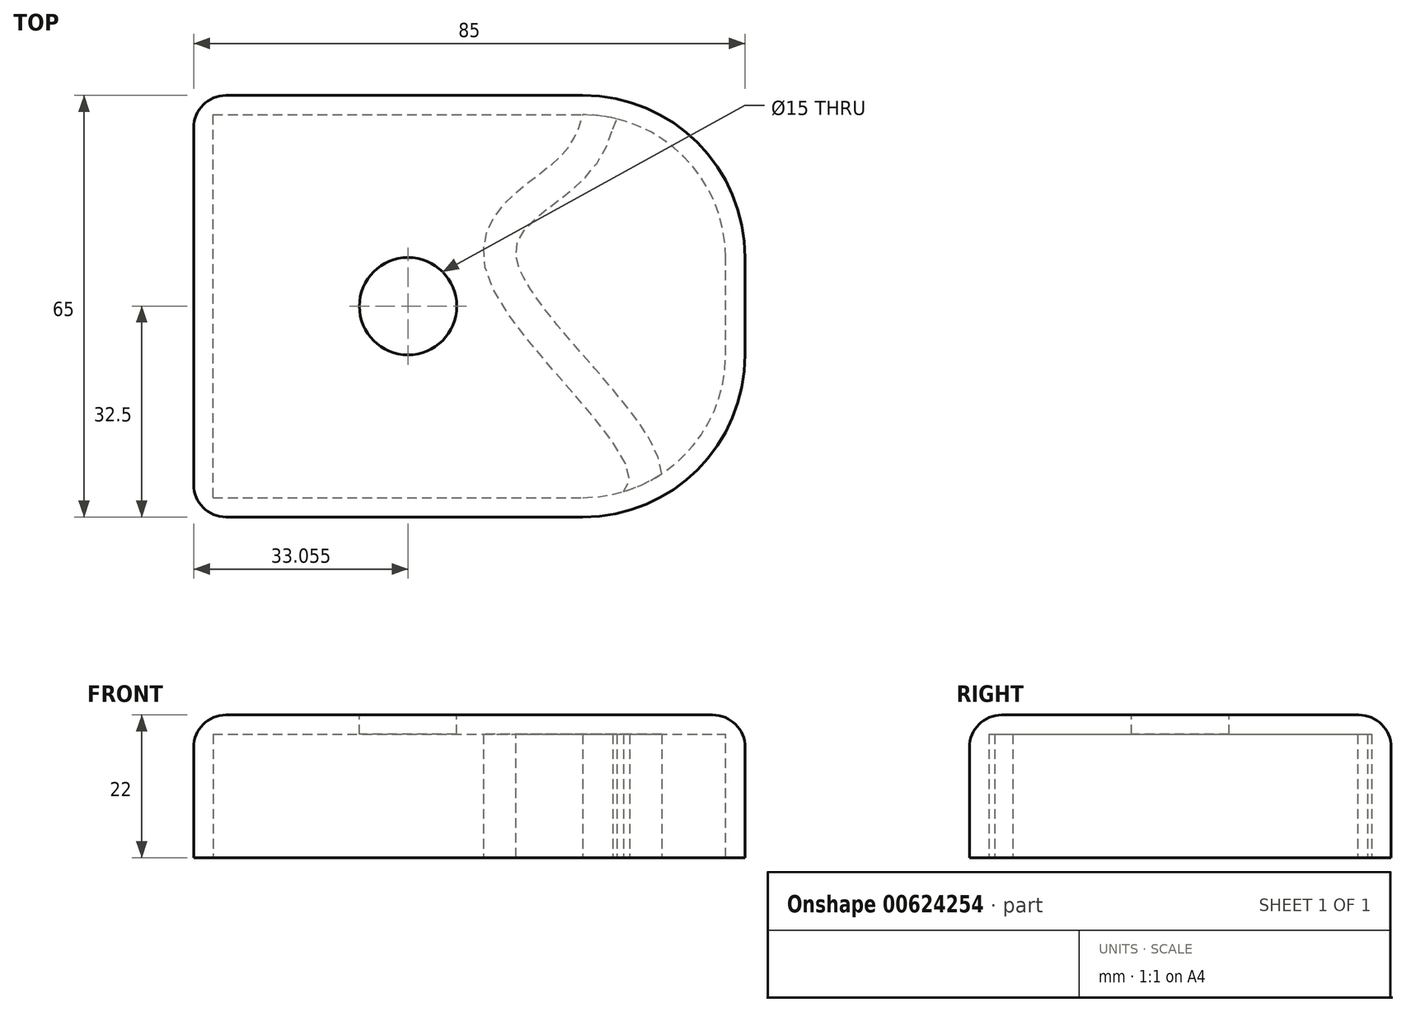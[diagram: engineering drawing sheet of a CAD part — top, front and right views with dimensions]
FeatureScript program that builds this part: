
annotation { "Feature Type Name" : "Feature", "Feature Type Description" : "" }
export const myFeature = defineFeature(function(context is Context, id is Id, definition is map)
    precondition{}
    {
        {
            var Q0;
            Q0=qCreatedBy(makeId("Top.planeOp"),FACE);
            var sketch = newSketch(context, id + "F0", { "sketchPlane" : qUnion([Q0])});
            skLineSegment(sketch, "E0.bottom", {"start": v(0, 0) * mm, "end": v(60, 0) * mm});
            skLineSegment(sketch, "E0.top", {"start": v(0, 65) * mm, "end": v(60, 65) * mm});
            skLineSegment(sketch, "E0.left", {"start": v(0, 0) * mm, "end": v(0, 65) * mm});
            skLineSegment(sketch, "E0.right", {"start": v(85, 25) * mm, "end": v(85, 40) * mm});
            skPoint(sketch, "E1.visualSharp", {"position": v(85, 65) * mm});
            skArc(sketch, "E1.filletArc", {"start": v(85, 40) * mm, "mid": v(77.68, 57.68) * mm, "end": v(60, 65) * mm});
            skPoint(sketch, "E2.visualSharp", {"position": v(85, 0) * mm});
            skArc(sketch, "E2.filletArc", {"start": v(60, 0) * mm, "mid": v(77.68, 7.32) * mm, "end": v(85, 25) * mm});
            skSolve(sketch);
        }
        {
            var Q0;
            Q0=makeQuery(id+"F0.imprint","IMPRINT",FACE,{"disambiguationData":[TD([[makeQuery(id+"F0.imprint","IMPRINT",EDGE,{"derivedFrom":sQuery(id+"F0.wireOp",EDGE,"E0.bottom")}),1.0]])]});
            extrude(context, id + "F1", {"entities" : qUnion([Q0]), "depth" : 22 * mm, "offsetDistance" : 25 * mm});
        }
        {
            var Q0;
            Q0=makeQuery(id+"F1.opExtrude","CAP_FACE",FACE,{"disambiguationData":[OSD([sQuery(id+"F0.wireOp",EDGE,"E0.bottom"),sQuery(id+"F0.wireOp",EDGE,"E0.top"),sQuery(id+"F0.wireOp",EDGE,"E0.left"),sQuery(id+"F0.wireOp",EDGE,"E0.right"),sQuery(id+"F0.wireOp",EDGE,"E1.filletArc"),sQuery(id+"F0.wireOp",EDGE,"E2.filletArc")])],"isStart":true});
            shell(context, id + "F2", {"entities" : qUnion([Q0]), "thickness" : 3 * mm});
        }
        {
            var Q0;
            Q0=makeQuery(id+"F1.opExtrude","SWEPT_EDGE",EDGE,{"disambiguationData":[OSD([sQuery(id+"F0.wireOp",EDGE,"E0.bottom"),sQuery(id+"F0.wireOp",EDGE,"E0.left")])]});
            fillet(context, id + "F3", {"entities" : qUnion([Q0]), "radius" : 5 * mm, "tangentPropagation" : true, "allowEdgeOverflow" : false});
        }
        {
            var Q0;
            Q0=makeQuery(id+"F1.opExtrude","SWEPT_EDGE",EDGE,{"disambiguationData":[OSD([sQuery(id+"F0.wireOp",EDGE,"E0.top"),sQuery(id+"F0.wireOp",EDGE,"E0.left")])]});
            fillet(context, id + "F4", {"entities" : qUnion([Q0]), "radius" : 5 * mm, "tangentPropagation" : true, "allowEdgeOverflow" : false});
        }
        {
            var Q0;
            Q0=makeQuery(id+"F1.opExtrude","CAP_EDGE",EDGE,{"disambiguationData":[OSD([sQuery(id+"F0.wireOp",EDGE,"E0.left")])],"isStart":false});
            fillet(context, id + "F5", {"entities" : qUnion([Q0]), "radius" : 5 * mm, "tangentPropagation" : true, "allowEdgeOverflow" : false});
        }
        {
            var Q0;
            Q0=qCreatedBy(makeId("Top.planeOp"),FACE);
            var sketch = newSketch(context, id + "F6", { "sketchPlane" : qUnion([Q0])});
            skLineSegment(sketch, "E3.0.0", {"start": v(82, 40) * mm, "end": v(82, 25) * mm});
            skArc(sketch, "E3.0.1", {"start": v(82, 25) * mm, "mid": v(75.56, 9.44) * mm, "end": v(60, 3) * mm});
            skLineSegment(sketch, "E3.0.3", {"start": v(3, 3) * mm, "end": v(3, 62) * mm});
            skLineSegment(sketch, "E3.0.4", {"start": v(3, 62) * mm, "end": v(60, 62) * mm});
            skArc(sketch, "E3.0.5", {"start": v(60, 62) * mm, "mid": v(75.56, 55.56) * mm, "end": v(82, 40) * mm});
            skFitSpline(sketch, "E4", {"points": [v(60, 3) * mm, v(46.08, 35.31) * mm, v(53.73, 53.21) * mm, v(60, 62) * mm], "startDerivative": vector(138.95, -9.54) * mm, "endDerivative": vector(13.37, 52.7) * mm});
            skFitSpline(sketch, "E5.0", {"points": [v(59.66, -1.99) * mm, v(60.5, -2.05) * mm, v(62.08, -2.1) * mm, v(64.25, -1.97) * mm, v(65.98, -1.64) * mm, v(67.35, -1.17) * mm, v(68.38, -0.68) * mm, v(69.4, -0.02) * mm, v(70.33, 0.85) * mm, v(71.13, 1.9) * mm, v(71.72, 3.1) * mm, v(72.07, 4.3) * mm, v(72.2, 5.48) * mm, v(72.18, 6.57) * mm, v(71.99, 7.9) * mm, v(71.54, 9.4) * mm, v(70.83, 11) * mm, v(69.97, 12.53) * mm, v(69, 14.03) * mm, v(67.9, 15.54) * mm, v(66.34, 17.58) * mm, v(64.2, 20.17) * mm, v(61.44, 23.35) * mm, v(58.65, 26.54) * mm, v(55.98, 29.68) * mm, v(54, 32.18) * mm, v(52.64, 34.05) * mm, v(51.76, 35.37) * mm, v(51.15, 36.38) * mm, v(50.76, 37.12) * mm, v(50.51, 37.62) * mm, v(50.3, 38.1) * mm, v(50.07, 38.7) * mm, v(49.87, 39.36) * mm, v(49.73, 40.06) * mm, v(49.66, 40.86) * mm, v(49.73, 41.7) * mm, v(50, 42.6) * mm, v(50.52, 43.58) * mm, v(51.3, 44.62) * mm, v(52.35, 45.7) * mm, v(53.59, 46.78) * mm, v(54.95, 47.86) * mm, v(56.14, 48.75) * mm, v(57.1, 49.5) * mm, v(57.8, 50.04) * mm, v(58.47, 50.6) * mm, v(59.35, 51.38) * mm, v(60.42, 52.4) * mm, v(61.6, 53.77) * mm, v(62.67, 55.3) * mm, v(63.57, 57) * mm, v(64.3, 58.81) * mm, v(64.68, 60.1) * mm, v(64.85, 60.77) * mm]});
            skFitSpline(sketch, "E6", {"points": [v(59.66, -1.99) * mm, v(60.5, -2.05) * mm, v(62.08, -2.1) * mm, v(64.25, -1.97) * mm, v(65.98, -1.64) * mm, v(67.35, -1.17) * mm, v(68.38, -0.68) * mm, v(69.4, -0.02) * mm, v(70.33, 0.85) * mm, v(71.13, 1.9) * mm, v(71.72, 3.1) * mm, v(72.07, 4.3) * mm, v(72.2, 5.48) * mm, v(72.18, 6.57) * mm, v(71.99, 7.9) * mm, v(71.54, 9.4) * mm, v(70.83, 11) * mm, v(69.97, 12.53) * mm, v(69, 14.03) * mm, v(67.9, 15.54) * mm, v(66.34, 17.58) * mm, v(64.2, 20.17) * mm, v(61.44, 23.35) * mm, v(58.65, 26.54) * mm, v(55.98, 29.68) * mm, v(54, 32.18) * mm, v(52.64, 34.05) * mm, v(51.76, 35.37) * mm, v(51.15, 36.38) * mm, v(50.76, 37.12) * mm, v(50.51, 37.62) * mm, v(50.3, 38.1) * mm, v(50.07, 38.7) * mm, v(49.87, 39.36) * mm, v(49.73, 40.06) * mm, v(49.66, 40.86) * mm, v(49.73, 41.7) * mm, v(50, 42.6) * mm, v(50.52, 43.58) * mm, v(51.3, 44.62) * mm, v(52.35, 45.7) * mm, v(53.59, 46.78) * mm, v(54.95, 47.86) * mm, v(56.14, 48.75) * mm, v(57.1, 49.5) * mm, v(57.8, 50.04) * mm, v(58.47, 50.6) * mm, v(59.35, 51.38) * mm, v(60.42, 52.4) * mm, v(61.6, 53.77) * mm, v(62.67, 55.3) * mm, v(63.57, 57) * mm, v(64.3, 58.81) * mm, v(64.68, 60.1) * mm, v(64.85, 60.77) * mm]});
            skFitSpline(sketch, "E7", {"points": [v(59.66, -1.99) * mm, v(60.5, -2.05) * mm, v(62.08, -2.1) * mm, v(64.25, -1.97) * mm, v(65.98, -1.64) * mm, v(67.35, -1.17) * mm, v(68.38, -0.68) * mm, v(69.4, -0.02) * mm, v(70.33, 0.85) * mm, v(71.13, 1.9) * mm, v(71.72, 3.1) * mm, v(72.07, 4.3) * mm, v(72.2, 5.48) * mm, v(72.18, 6.57) * mm, v(71.99, 7.9) * mm, v(71.54, 9.4) * mm, v(70.83, 11) * mm, v(69.97, 12.53) * mm, v(69, 14.03) * mm, v(67.9, 15.54) * mm, v(66.34, 17.58) * mm, v(64.2, 20.17) * mm, v(61.44, 23.35) * mm, v(58.65, 26.54) * mm, v(55.98, 29.68) * mm, v(54, 32.18) * mm, v(52.64, 34.05) * mm, v(51.76, 35.37) * mm, v(51.15, 36.38) * mm, v(50.76, 37.12) * mm, v(50.51, 37.62) * mm, v(50.3, 38.1) * mm, v(50.07, 38.7) * mm, v(49.87, 39.36) * mm, v(49.73, 40.06) * mm, v(49.66, 40.86) * mm, v(49.73, 41.7) * mm, v(50, 42.6) * mm, v(50.52, 43.58) * mm, v(51.3, 44.62) * mm, v(52.35, 45.7) * mm, v(53.59, 46.78) * mm, v(54.95, 47.86) * mm, v(56.14, 48.75) * mm, v(57.1, 49.5) * mm, v(57.8, 50.04) * mm, v(58.47, 50.6) * mm, v(59.35, 51.38) * mm, v(60.42, 52.4) * mm, v(61.6, 53.77) * mm, v(62.67, 55.3) * mm, v(63.57, 57) * mm, v(64.3, 58.81) * mm, v(64.68, 60.1) * mm, v(64.85, 60.77) * mm]});
            skLineSegment(sketch, "E8", {"start": v(64.55, 59.69) * mm, "end": v(65.26, 61.36) * mm});
            skSolve(sketch);
        }
        {
            var Q0;
            {var subQ4=sQuery(id+"F6.wireOp",EDGE,"E4");Q0=makeQuery(id+"F6.imprint","IMPRINT",FACE,{"disambiguationData":[TD([[makeQuery(id+"F6.imprint","IMPRINT",EDGE,{"derivedFrom":subQ4}),-1.0]])]});}
            extrude(context, id + "F7", {"entities" : qUnion([Q0]), "endBound" : BoundingType.UP_TO_NEXT, "depth" : 25 * mm, "offsetDistance" : 25 * mm});
        }
        {
            var Q0;
            Q0=makeQuery(id+"F1.opExtrude","CAP_FACE",FACE,{"disambiguationData":[OSD([sQuery(id+"F0.wireOp",EDGE,"E0.bottom"),sQuery(id+"F0.wireOp",EDGE,"E0.top"),sQuery(id+"F0.wireOp",EDGE,"E0.left"),sQuery(id+"F0.wireOp",EDGE,"E0.right"),sQuery(id+"F0.wireOp",EDGE,"E1.filletArc"),sQuery(id+"F0.wireOp",EDGE,"E2.filletArc")])],"isStart":false});
            var sketch = newSketch(context, id + "F8", { "sketchPlane" : qUnion([Q0])});
            skLineSegment(sketch, "E9", {"start": v(80, 32.5) * mm, "end": v(5, 32.5) * mm, "construction": true});
            skCircle(sketch, "E10", {"center": v(33.06, 32.5) * mm, "radius": 7.5 * mm});
            skSolve(sketch);
        }
        {
            var Q0;
            Q0=makeQuery(id+"F8.imprint","IMPRINT",FACE,{"disambiguationData":[TD([[makeQuery(id+"F8.imprint","IMPRINT",EDGE,{"derivedFrom":sQuery(id+"F8.wireOp",EDGE,"E10")}),1.0]])]});
            extrude(context, id + "F9", {"entities" : qUnion([Q0]), "operationType" : NewBodyOperationType.REMOVE, "oppositeDirection" : true, "depth" : 25 * mm, "offsetDistance" : 25 * mm});
        }
    });
